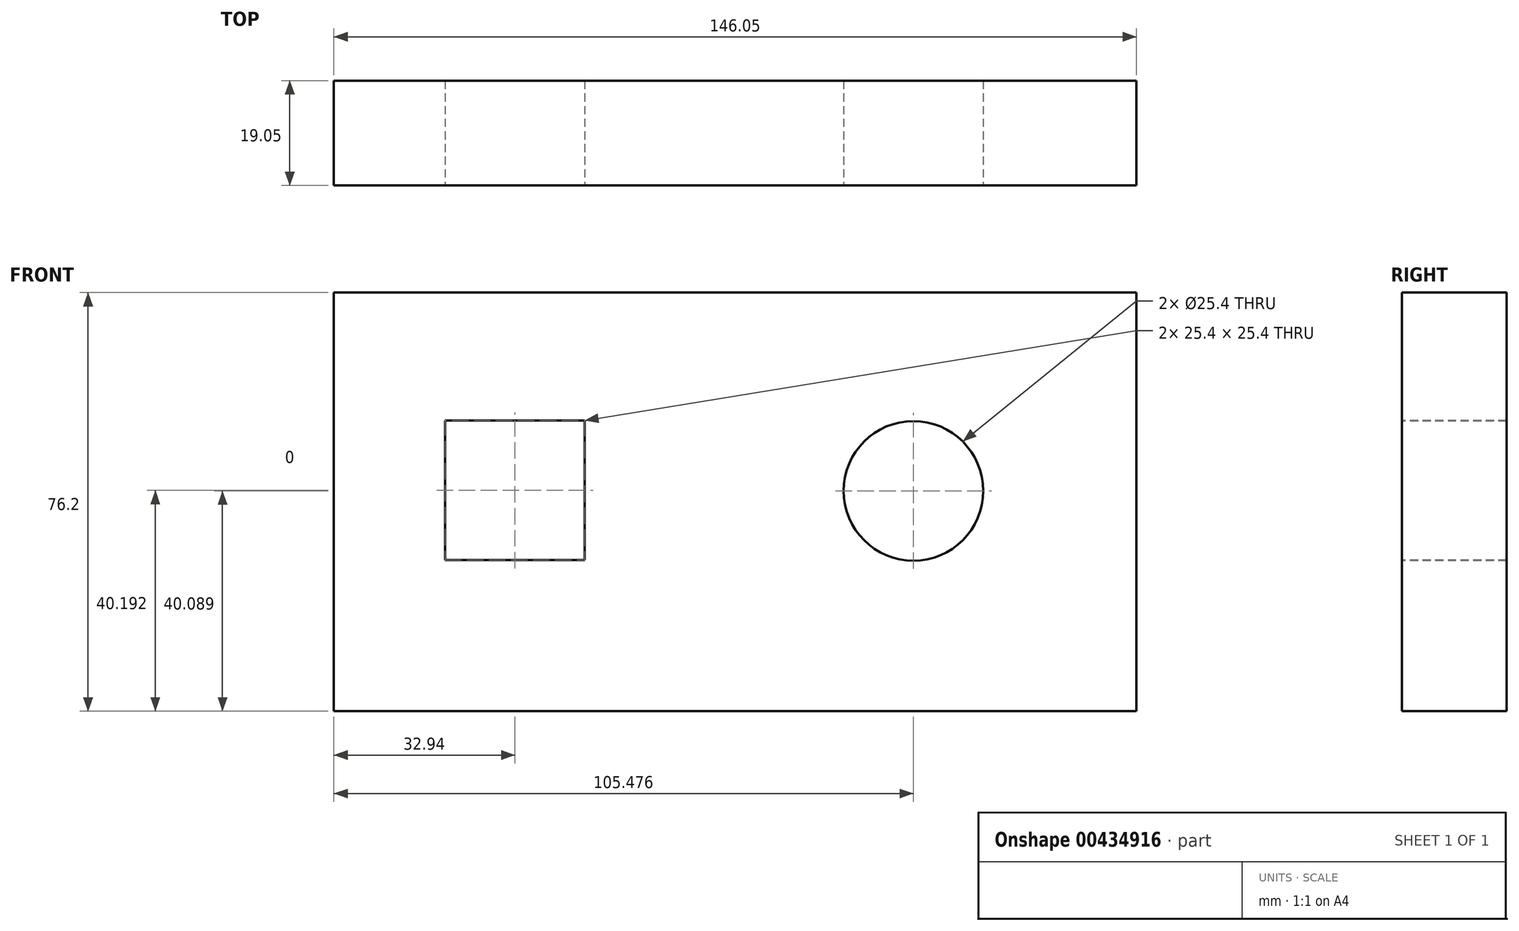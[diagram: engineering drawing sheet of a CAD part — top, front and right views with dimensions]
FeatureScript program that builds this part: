
annotation { "Feature Type Name" : "Feature", "Feature Type Description" : "" }
export const myFeature = defineFeature(function(context is Context, id is Id, definition is map)
    precondition{}
    {
        {
            var Q0;
            Q0=qCreatedBy(makeId("Front.planeOp"),FACE);
            var sketch = newSketch(context, id + "F0", { "sketchPlane" : qUnion([Q0])});
            skLineSegment(sketch, "E0", {"start": v(-69.85, -55.54) * mm, "end": v(76.2, -55.54) * mm});
            skLineSegment(sketch, "E1", {"start": v(76.2, -55.54) * mm, "end": v(76.2, 20.66) * mm});
            skLineSegment(sketch, "E2", {"start": v(76.2, 20.66) * mm, "end": v(-69.85, 20.66) * mm});
            skLineSegment(sketch, "E3", {"start": v(-69.85, 20.66) * mm, "end": v(-69.85, -55.54) * mm});
            skSolve(sketch);
        }
        {
            var Q0;
            Q0 = qSketchRegion(id + "F0", true);
            extrude(context, id + "F1", {"entities" : qUnion([Q0]), "depth" : 19.05 * mm});
        }
        {
            var Q0;
            Q0=makeQuery(id+"F1.opExtrude","CAP_FACE",FACE,{"disambiguationData":[OSD([sQuery(id+"F0.wireOp",EDGE,"E0"),sQuery(id+"F0.wireOp",EDGE,"E1"),sQuery(id+"F0.wireOp",EDGE,"E2"),sQuery(id+"F0.wireOp",EDGE,"E3")])],"isStart":false});
            var sketch = newSketch(context, id + "F2", { "sketchPlane" : qUnion([Q0])});
            skCircle(sketch, "E4", {"center": v(35.63, -15.45) * mm, "radius": 12.7 * mm});
            skSolve(sketch);
        }
        {
            var Q0;
            Q0 = qSketchRegion(id + "F2", true);
            extrude(context, id + "F3", {"entities" : qUnion([Q0]), "operationType" : NewBodyOperationType.REMOVE, "oppositeDirection" : true, "depth" : 19.05 * mm});
        }
        {
            var Q0;
            Q0=makeQuery(id+"F1.opExtrude","CAP_FACE",FACE,{"disambiguationData":[OSD([sQuery(id+"F0.wireOp",EDGE,"E0"),sQuery(id+"F0.wireOp",EDGE,"E1"),sQuery(id+"F0.wireOp",EDGE,"E2"),sQuery(id+"F0.wireOp",EDGE,"E3")])],"isStart":false});
            var sketch = newSketch(context, id + "F4", { "sketchPlane" : qUnion([Q0])});
            skLineSegment(sketch, "E5.bottom", {"start": v(-49.6, -2.65) * mm, "end": v(-24.2, -2.65) * mm});
            skLineSegment(sketch, "E5.top", {"start": v(-49.6, -28.05) * mm, "end": v(-24.2, -28.05) * mm});
            skLineSegment(sketch, "E5.left", {"start": v(-49.6, -2.65) * mm, "end": v(-49.6, -28.05) * mm});
            skLineSegment(sketch, "E5.right", {"start": v(-24.2, -2.65) * mm, "end": v(-24.2, -28.05) * mm});
            skSolve(sketch);
        }
        {
            var Q0;
            Q0 = qSketchRegion(id + "F4", true);
            extrude(context, id + "F5", {"entities" : qUnion([Q0]), "operationType" : NewBodyOperationType.REMOVE, "oppositeDirection" : true, "depth" : 19.05 * mm});
        }
    });
